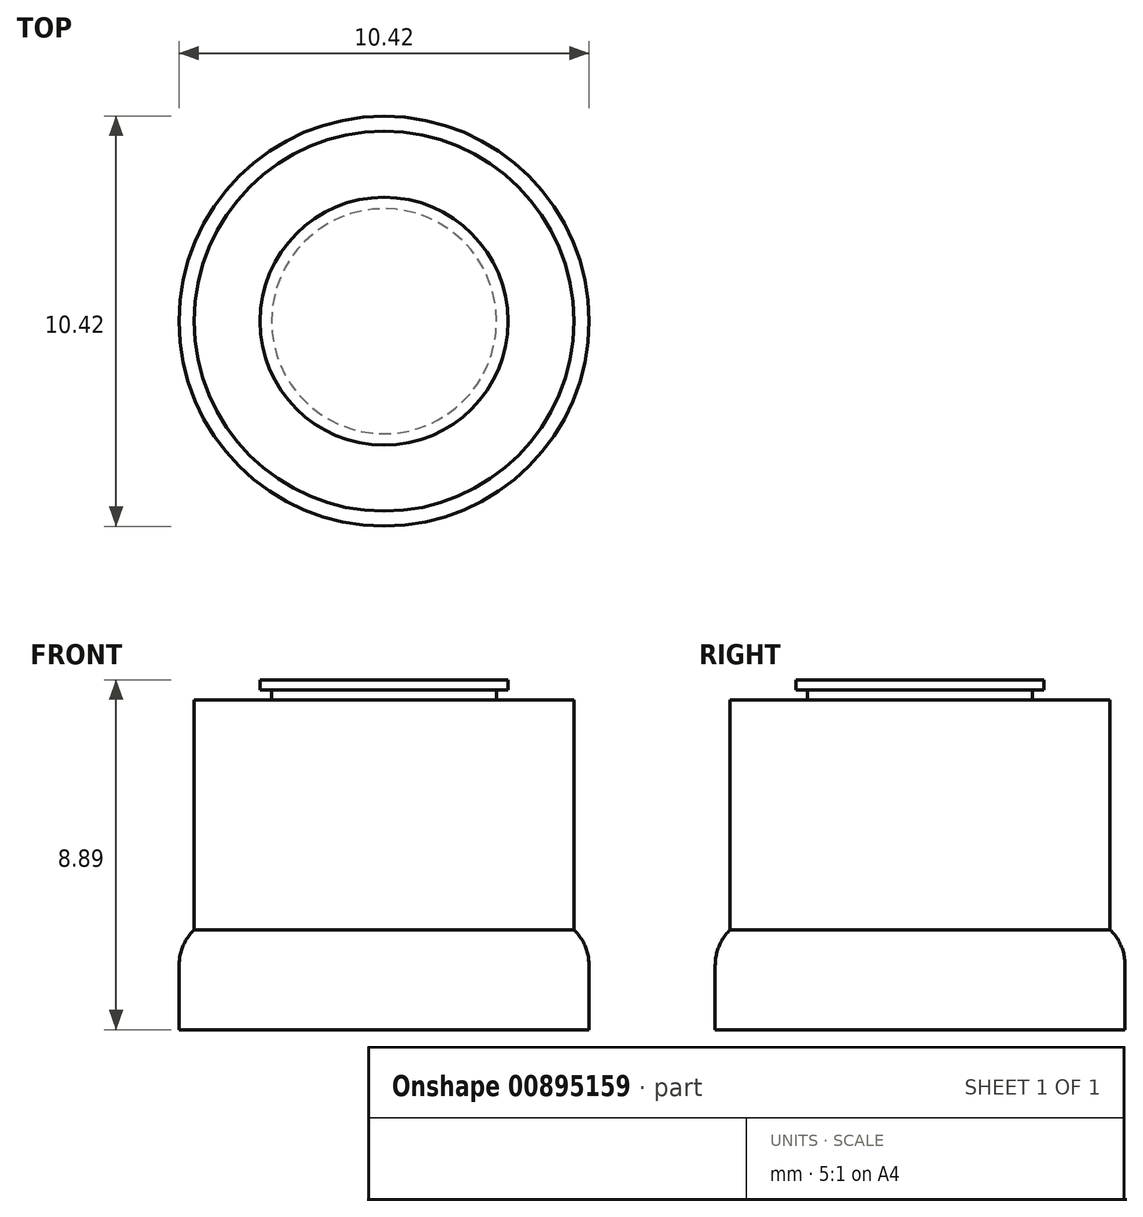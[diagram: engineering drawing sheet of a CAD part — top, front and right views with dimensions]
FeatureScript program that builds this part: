
annotation { "Feature Type Name" : "Feature", "Feature Type Description" : "" }
export const myFeature = defineFeature(function(context is Context, id is Id, definition is map)
    precondition{}
    {
        {
            var Q0;
            Q0=qCreatedBy(makeId("Top.planeOp"),FACE);
            var sketch = newSketch(context, id + "F0", { "sketchPlane" : qUnion([Q0])});
            skCircle(sketch, "E0", {"center": v(0, 0) * mm, "radius": 5.2 * mm});
            skSolve(sketch);
        }
        {
            var Q0;
            Q0=makeQuery(id+"F0.imprint","IMPRINT",FACE,{"disambiguationData":[TD([[makeQuery(id+"F0.imprint","IMPRINT",EDGE,{"derivedFrom":sQuery(id+"F0.wireOp",EDGE,"E0")}),1.0]])]});
            extrude(context, id + "F1", {"entities" : qUnion([Q0]), "depth" : 2.54 * mm, "offsetDistance" : 25.4 * mm});
        }
        {
            var Q0;
            Q0=makeQuery(id+"F1.opExtrude","CAP_FACE",FACE,{"disambiguationData":[OSD([sQuery(id+"F0.wireOp",EDGE,"E0")])],"isStart":false});
            var sketch = newSketch(context, id + "F2", { "sketchPlane" : qUnion([Q0])});
            skCircle(sketch, "E1", {"center": v(0, 0) * mm, "radius": 4.83 * mm});
            skSolve(sketch);
        }
        {
            var Q0;
            Q0 = qSketchRegion(id + "F2", true);
            extrude(context, id + "F3", {"entities" : qUnion([Q0]), "operationType" : NewBodyOperationType.ADD, "depth" : 5.84 * mm, "offsetDistance" : 25.4 * mm});
        }
        {
            var Q0;
            Q0=makeQuery(id+"F1.opExtrude","CAP_EDGE",EDGE,{"disambiguationData":[OSD([sQuery(id+"F0.wireOp",EDGE,"E0")])],"isStart":false});
            fillet(context, id + "F4", {"entities" : qUnion([Q0]), "radius" : 1.27 * mm, "tangentPropagation" : true, "allowEdgeOverflow" : false});
        }
        {
            var Q0;
            Q0=makeQuery(id+"F3.opExtrude","CAP_FACE",FACE,{"disambiguationData":[OSD([sQuery(id+"F2.wireOp",EDGE,"E1")])],"isStart":false});
            var sketch = newSketch(context, id + "F5", { "sketchPlane" : qUnion([Q0])});
            skCircle(sketch, "E2", {"center": v(0, 0) * mm, "radius": 2.86 * mm});
            skSolve(sketch);
        }
        {
            var Q0;
            Q0 = qSketchRegion(id + "F5", true);
            extrude(context, id + "F6", {"entities" : qUnion([Q0]), "operationType" : NewBodyOperationType.ADD, "depth" : 0.25 * mm, "offsetDistance" : 25.4 * mm});
        }
        {
            var Q0;
            Q0=makeQuery(id+"F6.opExtrude","CAP_FACE",FACE,{"disambiguationData":[OSD([sQuery(id+"F5.wireOp",EDGE,"E2")])],"isStart":false});
            var sketch = newSketch(context, id + "F7", { "sketchPlane" : qUnion([Q0])});
            skCircle(sketch, "E3", {"center": v(0, 0) * mm, "radius": 3.15 * mm});
            skSolve(sketch);
        }
        {
            var Q0;
            Q0 = qSketchRegion(id + "F7", true);
            extrude(context, id + "F8", {"entities" : qUnion([Q0]), "operationType" : NewBodyOperationType.ADD, "depth" : 0.25 * mm, "offsetDistance" : 25.4 * mm});
        }
    });
